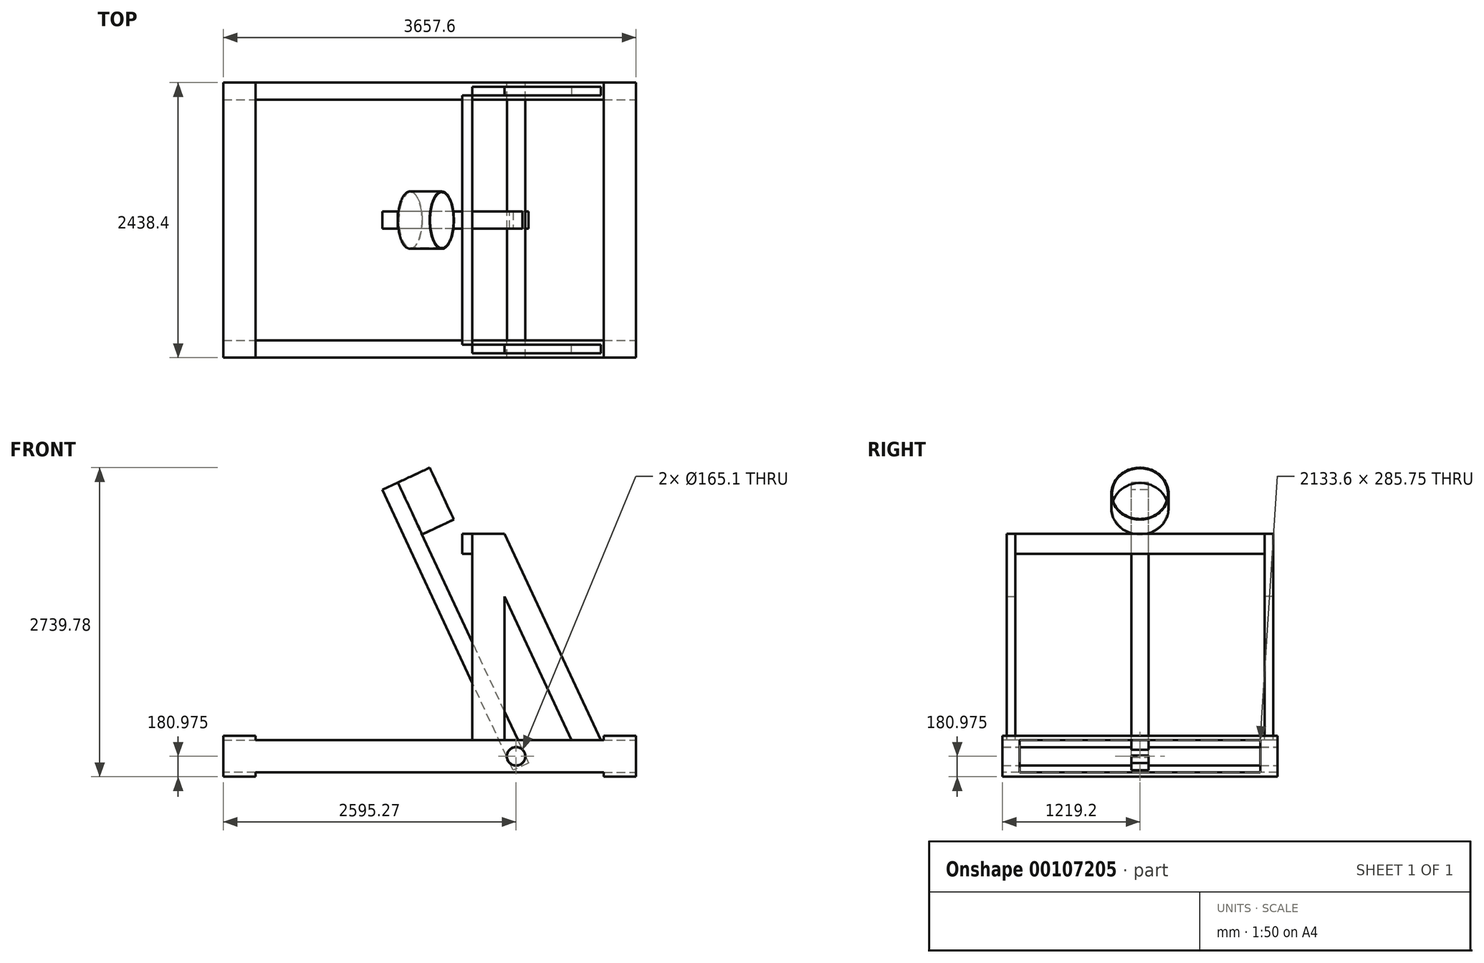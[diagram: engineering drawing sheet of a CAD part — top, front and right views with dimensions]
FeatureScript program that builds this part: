
annotation { "Feature Type Name" : "Feature", "Feature Type Description" : "" }
export const myFeature = defineFeature(function(context is Context, id is Id, definition is map)
    precondition{}
    {
        {
            var Q0;
            Q0=qCreatedBy(makeId("Front.planeOp"),FACE);
            var sketch = newSketch(context, id + "F0", { "sketchPlane" : qUnion([Q0])});
            skLineSegment(sketch, "E0.bottom", {"start": v(0, 0) * mm, "end": v(3657.6, 0) * mm});
            skLineSegment(sketch, "E0.top", {"start": v(0, 285.75) * mm, "end": v(3657.6, 285.75) * mm});
            skLineSegment(sketch, "E0.left", {"start": v(0, 0) * mm, "end": v(0, 285.75) * mm});
            skLineSegment(sketch, "E0.right", {"start": v(3657.6, 0) * mm, "end": v(3657.6, 285.75) * mm});
            skSolve(sketch);
        }
        {
            var Q0;
            Q0 = qSketchRegion(id + "F0", true);
            extrude(context, id + "F1", {"entities" : qUnion([Q0]), "oppositeDirection" : true, "depth" : 152.4 * mm});
        }
        {
            var Q0;
            Q0=makeQuery(id+"F1.opExtrude","SWEPT_FACE",FACE,{"disambiguationData":[OSD([sQuery(id+"F0.wireOp",EDGE,"E0.top")])]});
            var sketch = newSketch(context, id + "F2", { "sketchPlane" : qUnion([Q0])});
            skLineSegment(sketch, "E1.bottom", {"start": v(0, 152.4) * mm, "end": v(285.75, 152.4) * mm});
            skLineSegment(sketch, "E1.top", {"start": v(0, -2286) * mm, "end": v(285.75, -2286) * mm});
            skLineSegment(sketch, "E1.left", {"start": v(0, 152.4) * mm, "end": v(0, -2286) * mm});
            skLineSegment(sketch, "E1.right", {"start": v(285.75, 152.4) * mm, "end": v(285.75, -2286) * mm});
            skSolve(sketch);
        }
        {
            var Q0;
            Q0 = qSketchRegion(id + "F2", true);
            extrude(context, id + "F3", {"entities" : qUnion([Q0]), "operationType" : NewBodyOperationType.ADD, "depth" : 38.1 * mm});
        }
        {
            var Q0;
            Q0=makeQuery(id+"F1.opExtrude","SWEPT_FACE",FACE,{"disambiguationData":[OSD([sQuery(id+"F0.wireOp",EDGE,"E0.bottom")])]});
            var sketch = newSketch(context, id + "F4", { "sketchPlane" : qUnion([Q0])});
            skLineSegment(sketch, "E2.0.0", {"start": v(0, 2286) * mm, "end": v(0, 0) * mm});
            skLineSegment(sketch, "E2.0.1", {"start": v(0, 0) * mm, "end": v(285.75, 0) * mm});
            skLineSegment(sketch, "E2.0.2", {"start": v(285.75, 0) * mm, "end": v(285.75, 2286) * mm});
            skLineSegment(sketch, "E2.0.3", {"start": v(285.75, 2286) * mm, "end": v(0, 2286) * mm});
            skLineSegment(sketch, "E3.0.0", {"start": v(0, -152.4) * mm, "end": v(0, 2286) * mm});
            skLineSegment(sketch, "E3.0.1", {"start": v(0, 2286) * mm, "end": v(285.75, 2286) * mm});
            skLineSegment(sketch, "E3.0.2", {"start": v(285.75, 2286) * mm, "end": v(285.75, -152.4) * mm});
            skLineSegment(sketch, "E3.0.3", {"start": v(285.75, -152.4) * mm, "end": v(0, -152.4) * mm});
            skSolve(sketch);
        }
        {
            var Q0;
            Q0 = qSketchRegion(id + "F4", true);
            extrude(context, id + "F5", {"entities" : qUnion([Q0]), "operationType" : NewBodyOperationType.ADD, "depth" : 38.1 * mm});
        }
        {
            var Q0;
            Q0=makeQuery(id+"F3.opExtrude","SWEPT_FACE",FACE,{"disambiguationData":[OSD([sQuery(id+"F2.wireOp",EDGE,"E1.top")])]});
            var sketch = newSketch(context, id + "F6", { "sketchPlane" : qUnion([Q0])});
            skLineSegment(sketch, "E4.0.0", {"start": v(0, -38.1) * mm, "end": v(0, 323.85) * mm});
            skLineSegment(sketch, "E4.0.1", {"start": v(0, 323.85) * mm, "end": v(285.75, 323.85) * mm});
            skLineSegment(sketch, "E4.0.2", {"start": v(285.75, 323.85) * mm, "end": v(285.75, 285.75) * mm});
            skLineSegment(sketch, "E4.0.3", {"start": v(285.75, 285.75) * mm, "end": v(3657.6, 285.75) * mm});
            skLineSegment(sketch, "E4.0.4", {"start": v(3657.6, 285.75) * mm, "end": v(3657.6, 0) * mm});
            skLineSegment(sketch, "E4.0.5", {"start": v(3657.6, 0) * mm, "end": v(285.75, 0) * mm});
            skLineSegment(sketch, "E4.0.6", {"start": v(285.75, 0) * mm, "end": v(285.75, -38.1) * mm});
            skLineSegment(sketch, "E4.0.7", {"start": v(285.75, -38.1) * mm, "end": v(0, -38.1) * mm});
            skSolve(sketch);
        }
        {
            var Q0;
            {var subQ2=sQuery(id+"F6.wireOp",EDGE,"E4.0.1");Q0=makeQuery(id+"F6.imprint","IMPRINT",FACE,{"disambiguationData":[TD([[makeQuery(id+"F6.imprint","IMPRINT",EDGE,{"derivedFrom":subQ2}),-1.0]])]});}
            var Q1;
            Q1=makeQuery(id+"F6.imprint","IMPRINT",FACE,{"disambiguationData":[TD([[makeQuery(id+"F6.imprint","IMPRINT",EDGE,{"derivedFrom":sQuery(id+"F6.wireOp",EDGE,"E4.0.3")}),-1.0]])]});
            extrude(context, id + "F7", {"entities" : qUnion([Q0, Q1]), "operationType" : NewBodyOperationType.ADD, "oppositeDirection" : true, "depth" : 152.4 * mm});
        }
        {
            var Q0;
            Q0=makeQuery(id+"F7.opExtrude","SWEPT_FACE",FACE,{"disambiguationData":[OSD([sQuery(id+"F6.wireOp",EDGE,"E4.0.4")])]});
            var sketch = newSketch(context, id + "F8", { "sketchPlane" : qUnion([Q0])});
            skLineSegment(sketch, "E5.0.0", {"start": v(-2286, -38.1) * mm, "end": v(152.4, -38.1) * mm});
            skLineSegment(sketch, "E5.0.1", {"start": v(152.4, -38.1) * mm, "end": v(152.4, 0) * mm});
            skLineSegment(sketch, "E5.0.2", {"start": v(152.4, 0) * mm, "end": v(0, 0) * mm});
            skLineSegment(sketch, "E5.0.3", {"start": v(0, 0) * mm, "end": v(-2133.6, 0) * mm});
            skLineSegment(sketch, "E5.0.4", {"start": v(-2133.6, 0) * mm, "end": v(-2286, 0) * mm});
            skLineSegment(sketch, "E5.0.5", {"start": v(-2286, 0) * mm, "end": v(-2286, -38.1) * mm});
            skLineSegment(sketch, "E6.0.0", {"start": v(-2286, 285.75) * mm, "end": v(-2133.6, 285.75) * mm});
            skLineSegment(sketch, "E6.0.1", {"start": v(-2133.6, 285.75) * mm, "end": v(0, 285.75) * mm});
            skLineSegment(sketch, "E6.0.2", {"start": v(0, 285.75) * mm, "end": v(152.4, 285.75) * mm});
            skLineSegment(sketch, "E6.0.3", {"start": v(152.4, 285.75) * mm, "end": v(152.4, 323.85) * mm});
            skLineSegment(sketch, "E6.0.4", {"start": v(152.4, 323.85) * mm, "end": v(-2286, 323.85) * mm});
            skLineSegment(sketch, "E6.0.5", {"start": v(-2286, 323.85) * mm, "end": v(-2286, 285.75) * mm});
            skSolve(sketch);
        }
        {
            var Q0;
            Q0 = qSketchRegion(id + "F8", true);
            extrude(context, id + "F9", {"entities" : qUnion([Q0]), "operationType" : NewBodyOperationType.ADD, "oppositeDirection" : true, "depth" : 285.75 * mm});
        }
        {
            var Q0;
            Q0=makeQuery(id+"F7.opExtrude","CAP_FACE",FACE,{"disambiguationData":[OSD([sQuery(id+"F6.wireOp",EDGE,"E4.0.0"),sQuery(id+"F6.wireOp",EDGE,"E4.0.1"),sQuery(id+"F6.wireOp",EDGE,"E4.0.2"),sQuery(id+"F6.wireOp",EDGE,"E4.0.3"),sQuery(id+"F6.wireOp",EDGE,"E4.0.4"),sQuery(id+"F6.wireOp",EDGE,"E4.0.5"),sQuery(id+"F6.wireOp",EDGE,"E4.0.6"),sQuery(id+"F6.wireOp",EDGE,"E4.0.7")])],"isStart":false});
            var sketch = newSketch(context, id + "F10", { "sketchPlane" : qUnion([Q0])});
            skLineSegment(sketch, "E7.0.0", {"start": v(0, 0) * mm, "end": v(0, 285.75) * mm});
            skLineSegment(sketch, "E7.0.1", {"start": v(0, 285.75) * mm, "end": v(-285.75, 285.75) * mm});
            skLineSegment(sketch, "E7.0.2", {"start": v(-285.75, 285.75) * mm, "end": v(-3371.85, 285.75) * mm});
            skLineSegment(sketch, "E7.0.3", {"start": v(-3371.85, 285.75) * mm, "end": v(-3657.6, 285.75) * mm});
            skLineSegment(sketch, "E7.0.4", {"start": v(-3657.6, 285.75) * mm, "end": v(-3657.6, 0) * mm});
            skLineSegment(sketch, "E7.0.5", {"start": v(-3657.6, 0) * mm, "end": v(-3371.85, 0) * mm});
            skLineSegment(sketch, "E7.0.6", {"start": v(-3371.85, 0) * mm, "end": v(-285.75, 0) * mm});
            skLineSegment(sketch, "E7.0.7", {"start": v(-285.75, 0) * mm, "end": v(0, 0) * mm});
            skLineSegment(sketch, "E8", {"start": v(-2493.67, 2114.55) * mm, "end": v(-2493.67, 0) * mm});
            skLineSegment(sketch, "E9", {"start": v(-2493.67, 2114.55) * mm, "end": v(-2207.92, 2114.55) * mm});
            skLineSegment(sketch, "E10", {"start": v(-2207.92, 2114.55) * mm, "end": v(-2207.92, 0) * mm});
            skLineSegment(sketch, "E11", {"start": v(-2207.92, 0) * mm, "end": v(-2493.67, 0) * mm});
            skLineSegment(sketch, "E12", {"start": v(-3346.45, 285.75) * mm, "end": v(-2493.67, 2114.55) * mm});
            skLineSegment(sketch, "E13", {"start": v(-3346.45, 285.75) * mm, "end": v(-3479.7, 0) * mm});
            skLineSegment(sketch, "E14", {"start": v(-3220.46, 0) * mm, "end": v(-2493.67, 1558.61) * mm});
            skSolve(sketch);
        }
        {
            var Q0;
            {var subQ0=sQuery(id+"F10.wireOp",EDGE,"E9");Q0=makeQuery(id+"F10.imprint","IMPRINT",FACE,{"disambiguationData":[TD([[makeQuery(id+"F10.imprint","IMPRINT",EDGE,{"derivedFrom":subQ0}),-1.0]])]});}
            var Q1;
            {var subQ5=sQuery(id+"F10.wireOp",EDGE,"E11");Q1=makeQuery(id+"F10.imprint","IMPRINT",FACE,{"disambiguationData":[TD([[makeQuery(id+"F10.imprint","IMPRINT",EDGE,{"derivedFrom":subQ5}),1.0]])]});}
            var Q2;
            {var subQ0=sQuery(id+"F10.wireOp",EDGE,"E13");Q2=makeQuery(id+"F10.imprint","IMPRINT",FACE,{"disambiguationData":[TD([[makeQuery(id+"F10.imprint","IMPRINT",EDGE,{"derivedFrom":subQ0}),1.0]])]});}
            var Q3;
            {var subQ0=sQuery(id+"F10.wireOp",EDGE,"E12");Q3=makeQuery(id+"F10.imprint","IMPRINT",FACE,{"disambiguationData":[TD([[makeQuery(id+"F10.imprint","IMPRINT",EDGE,{"derivedFrom":subQ0}),-1.0]])]});}
            extrude(context, id + "F11", {"entities" : qUnion([Q0, Q1, Q2, Q3]), "operationType" : NewBodyOperationType.ADD, "oppositeDirection" : true, "depth" : 114.3 * mm});
        }
        {
            var Q0;
            {var subQ0=sQuery(id+"F10.wireOp",EDGE,"E12");Q0=makeQuery(id+"F10.imprint","IMPRINT",FACE,{"disambiguationData":[TD([[makeQuery(id+"F10.imprint","IMPRINT",EDGE,{"derivedFrom":subQ0}),-1.0]])]});}
            var Q1;
            {var subQ0=sQuery(id+"F10.wireOp",EDGE,"E9");Q1=makeQuery(id+"F10.imprint","IMPRINT",FACE,{"disambiguationData":[TD([[makeQuery(id+"F10.imprint","IMPRINT",EDGE,{"derivedFrom":subQ0}),-1.0]])]});}
            extrude(context, id + "F12", {"entities" : qUnion([Q0, Q1]), "operationType" : NewBodyOperationType.REMOVE, "oppositeDirection" : true, "depth" : 38.1 * mm});
        }
        {
            var Q0;
            Q0=makeQuery(id+"F1.opExtrude","CAP_FACE",FACE,{"disambiguationData":[OSD([sQuery(id+"F0.wireOp",EDGE,"E0.bottom"),sQuery(id+"F0.wireOp",EDGE,"E0.top"),sQuery(id+"F0.wireOp",EDGE,"E0.left"),sQuery(id+"F0.wireOp",EDGE,"E0.right")])],"isStart":true});
            var sketch = newSketch(context, id + "F13", { "sketchPlane" : qUnion([Q0])});
            skLineSegment(sketch, "E15.0.0", {"start": v(2207.92, 2114.55) * mm, "end": v(2207.92, 285.75) * mm});
            skLineSegment(sketch, "E15.0.1", {"start": v(2207.92, 285.75) * mm, "end": v(2493.67, 285.75) * mm});
            skLineSegment(sketch, "E15.0.2", {"start": v(2493.67, 285.75) * mm, "end": v(2493.67, 1558.61) * mm});
            skLineSegment(sketch, "E15.0.3", {"start": v(2493.67, 1558.61) * mm, "end": v(3087.21, 285.75) * mm});
            skLineSegment(sketch, "E15.0.4", {"start": v(3087.21, 285.75) * mm, "end": v(3346.45, 285.75) * mm});
            skLineSegment(sketch, "E15.0.5", {"start": v(3346.45, 285.75) * mm, "end": v(2493.67, 2114.55) * mm});
            skLineSegment(sketch, "E15.0.6", {"start": v(2493.67, 2114.55) * mm, "end": v(2207.92, 2114.55) * mm});
            skSolve(sketch);
        }
        {
            var Q0;
            Q0 = qSketchRegion(id + "F13", true);
            extrude(context, id + "F14", {"entities" : qUnion([Q0]), "operationType" : NewBodyOperationType.ADD, "oppositeDirection" : true, "depth" : 114.3 * mm});
        }
        {
            var Q0;
            Q0=makeQuery(id+"F14.boolean.opBoolean","MERGE",FACE,{"derivedFrom":[makeQuery(id+"F1.opExtrude","CAP_FACE",FACE,{"disambiguationData":[OSD([sQuery(id+"F0.wireOp",EDGE,"E0.bottom"),sQuery(id+"F0.wireOp",EDGE,"E0.top"),sQuery(id+"F0.wireOp",EDGE,"E0.left"),sQuery(id+"F0.wireOp",EDGE,"E0.right")])],"isStart":true}),makeQuery(id+"F14.opExtrude","CAP_FACE",FACE,{"disambiguationData":[OSD([sQuery(id+"F13.wireOp",EDGE,"E15.0.0"),sQuery(id+"F13.wireOp",EDGE,"E15.0.1"),sQuery(id+"F13.wireOp",EDGE,"E15.0.2"),sQuery(id+"F13.wireOp",EDGE,"E15.0.3"),sQuery(id+"F13.wireOp",EDGE,"E15.0.4"),sQuery(id+"F13.wireOp",EDGE,"E15.0.5"),sQuery(id+"F13.wireOp",EDGE,"E15.0.6")])],"isStart":true})]});
            var sketch = newSketch(context, id + "F15", { "sketchPlane" : qUnion([Q0])});
            skLineSegment(sketch, "E16.0.0", {"start": v(2207.92, 2114.55) * mm, "end": v(2207.92, 285.75) * mm});
            skLineSegment(sketch, "E16.0.1", {"start": v(2207.92, 285.75) * mm, "end": v(2493.67, 285.75) * mm});
            skLineSegment(sketch, "E16.0.2", {"start": v(2493.67, 285.75) * mm, "end": v(2493.67, 1558.61) * mm});
            skLineSegment(sketch, "E16.0.3", {"start": v(2493.67, 1558.61) * mm, "end": v(3087.21, 285.75) * mm});
            skLineSegment(sketch, "E16.0.4", {"start": v(3087.21, 285.75) * mm, "end": v(3346.45, 285.75) * mm});
            skLineSegment(sketch, "E16.0.5", {"start": v(3346.45, 285.75) * mm, "end": v(2493.67, 2114.55) * mm});
            skLineSegment(sketch, "E16.0.6", {"start": v(2493.67, 2114.55) * mm, "end": v(2207.92, 2114.55) * mm});
            skSolve(sketch);
        }
        {
            var Q0;
            Q0=makeQuery(id+"F15.imprint","IMPRINT",FACE,{"disambiguationData":[TD([[makeQuery(id+"F15.imprint","IMPRINT",EDGE,{"derivedFrom":sQuery(id+"F15.wireOp",EDGE,"E16.0.0")}),1.0]])]});
            extrude(context, id + "F16", {"entities" : qUnion([Q0]), "operationType" : NewBodyOperationType.REMOVE, "oppositeDirection" : true, "depth" : 38.1 * mm});
        }
        {
            var Q0;
            Q0=makeQuery(id+"F14.opExtrude","SWEPT_FACE",FACE,{"disambiguationData":[OSD([sQuery(id+"F13.wireOp",EDGE,"E15.0.0")])]});
            var sketch = newSketch(context, id + "F17", { "sketchPlane" : qUnion([Q0])});
            skLineSegment(sketch, "E17.0.0", {"start": v(-38.1, 285.75) * mm, "end": v(-38.1, 2114.55) * mm});
            skLineSegment(sketch, "E17.0.1", {"start": v(-38.1, 2114.55) * mm, "end": v(-114.3, 2114.55) * mm});
            skLineSegment(sketch, "E17.0.2", {"start": v(-114.3, 2114.55) * mm, "end": v(-114.3, 285.75) * mm});
            skLineSegment(sketch, "E17.0.3", {"start": v(-114.3, 285.75) * mm, "end": v(-38.1, 285.75) * mm});
            skLineSegment(sketch, "E18.0.0", {"start": v(2247.9, 2114.55) * mm, "end": v(2171.7, 2114.55) * mm});
            skLineSegment(sketch, "E18.0.1", {"start": v(2171.7, 2114.55) * mm, "end": v(2171.7, 285.75) * mm});
            skLineSegment(sketch, "E18.0.2", {"start": v(2171.7, 285.75) * mm, "end": v(2247.9, 285.75) * mm});
            skLineSegment(sketch, "E18.0.3", {"start": v(2247.9, 285.75) * mm, "end": v(2247.9, 2114.55) * mm});
            skLineSegment(sketch, "E19.bottom", {"start": v(-114.3, 2114.55) * mm, "end": v(2247.9, 2114.55) * mm});
            skLineSegment(sketch, "E19.top", {"start": v(-114.3, 1936.75) * mm, "end": v(2247.9, 1936.75) * mm});
            skLineSegment(sketch, "E19.left", {"start": v(-114.3, 2114.55) * mm, "end": v(-114.3, 1936.75) * mm});
            skLineSegment(sketch, "E19.right", {"start": v(2247.9, 2114.55) * mm, "end": v(2247.9, 1936.75) * mm});
            skSolve(sketch);
        }
        {
            var Q0;
            {var subQ5=sQuery(id+"F17.wireOp",EDGE,"E19.left");Q0=makeQuery(id+"F17.imprint","IMPRINT",FACE,{"disambiguationData":[TD([[makeQuery(id+"F17.imprint","IMPRINT",EDGE,{"derivedFrom":subQ5}),1.0]])]});}
            var Q1;
            {var subQ5=sQuery(id+"F17.wireOp",EDGE,"E19.right");Q1=makeQuery(id+"F17.imprint","IMPRINT",FACE,{"disambiguationData":[TD([[makeQuery(id+"F17.imprint","IMPRINT",EDGE,{"derivedFrom":subQ5}),-1.0]])]});}
            var Q2;
            {var subQ0=sQuery(id+"F17.wireOp",EDGE,"E19.bottom");var subQ1=sQuery(id+"F17.wireOp",EDGE,"E17.0.0");var subQ2=makeQuery(id+"F17.imprint","INTERSECT",VERTEX,{"derivedFrom":[subQ1,subQ0]});Q2=makeQuery(id+"F17.imprint","IMPRINT",FACE,{"disambiguationData":[TD([[makeQuery(id+"F17.imprint","IMPRINT",EDGE,{"disambiguationData":[TD([[subQ2,-1.0]])],"derivedFrom":subQ1}),1.0]])]});}
            extrude(context, id + "F18", {"entities" : qUnion([Q0, Q1, Q2]), "operationType" : NewBodyOperationType.ADD, "depth" : 88.9 * mm});
        }
        {
            var Q0;
            Q0=makeQuery(id+"F9.boolean.opBoolean","MERGE",FACE,{"derivedFrom":[makeQuery(id+"F5.boolean.opBoolean","MERGE",FACE,{"derivedFrom":[makeQuery(id+"F3.boolean.opBoolean","MERGE",FACE,{"derivedFrom":[makeQuery(id+"F1.opExtrude","CAP_FACE",FACE,{"disambiguationData":[OSD([sQuery(id+"F0.wireOp",EDGE,"E0.bottom"),sQuery(id+"F0.wireOp",EDGE,"E0.top"),sQuery(id+"F0.wireOp",EDGE,"E0.left"),sQuery(id+"F0.wireOp",EDGE,"E0.right")])],"isStart":false}),makeQuery(id+"F3.opExtrude","SWEPT_FACE",FACE,{"disambiguationData":[OSD([sQuery(id+"F2.wireOp",EDGE,"E1.bottom")])]})]}),makeQuery(id+"F5.opExtrude","SWEPT_FACE",FACE,{"disambiguationData":[OSD([sQuery(id+"F4.wireOp",EDGE,"E3.0.3")])]})]}),makeQuery(id+"F9.opExtrude","SWEPT_FACE",FACE,{"disambiguationData":[OSD([sQuery(id+"F8.wireOp",EDGE,"E5.0.1")])]}),makeQuery(id+"F9.opExtrude","SWEPT_FACE",FACE,{"disambiguationData":[OSD([sQuery(id+"F8.wireOp",EDGE,"E6.0.3")])]})]});
            var sketch = newSketch(context, id + "F19", { "sketchPlane" : qUnion([Q0])});
            skLineSegment(sketch, "E20.0.0", {"start": v(0, -38.1) * mm, "end": v(0, 323.85) * mm});
            skLineSegment(sketch, "E20.0.1", {"start": v(0, 323.85) * mm, "end": v(-285.75, 323.85) * mm});
            skLineSegment(sketch, "E20.0.2", {"start": v(-285.75, 323.85) * mm, "end": v(-285.75, 285.75) * mm});
            skLineSegment(sketch, "E20.0.3", {"start": v(-285.75, 285.75) * mm, "end": v(-3371.85, 285.75) * mm});
            skLineSegment(sketch, "E20.0.4", {"start": v(-3371.85, 285.75) * mm, "end": v(-3371.85, 323.85) * mm});
            skLineSegment(sketch, "E20.0.5", {"start": v(-3371.85, 323.85) * mm, "end": v(-3657.6, 323.85) * mm});
            skLineSegment(sketch, "E20.0.6", {"start": v(-3657.6, 323.85) * mm, "end": v(-3657.6, -38.1) * mm});
            skLineSegment(sketch, "E20.0.7", {"start": v(-3657.6, -38.1) * mm, "end": v(-3371.85, -38.1) * mm});
            skLineSegment(sketch, "E20.0.8", {"start": v(-3371.85, -38.1) * mm, "end": v(-3371.85, 0) * mm});
            skLineSegment(sketch, "E20.0.9", {"start": v(-3371.85, 0) * mm, "end": v(-285.75, 0) * mm});
            skLineSegment(sketch, "E20.0.10", {"start": v(-285.75, 0) * mm, "end": v(-285.75, -38.1) * mm});
            skLineSegment(sketch, "E20.0.11", {"start": v(-285.75, -38.1) * mm, "end": v(0, -38.1) * mm});
            skLineSegment(sketch, "E21.0.0", {"start": v(-2119.02, 2114.55) * mm, "end": v(-2493.67, 2114.55) * mm});
            skLineSegment(sketch, "E21.0.1", {"start": v(-2493.67, 2114.55) * mm, "end": v(-3346.45, 285.75) * mm});
            skLineSegment(sketch, "E21.0.2", {"start": v(-3346.45, 285.75) * mm, "end": v(-3087.21, 285.75) * mm});
            skLineSegment(sketch, "E21.0.3", {"start": v(-3087.21, 285.75) * mm, "end": v(-2493.67, 1558.61) * mm});
            skLineSegment(sketch, "E21.0.4", {"start": v(-2493.67, 1558.61) * mm, "end": v(-2493.67, 285.75) * mm});
            skLineSegment(sketch, "E21.0.5", {"start": v(-2493.67, 285.75) * mm, "end": v(-2207.92, 285.75) * mm});
            skLineSegment(sketch, "E21.0.6", {"start": v(-2207.92, 285.75) * mm, "end": v(-2207.92, 1936.75) * mm});
            skLineSegment(sketch, "E21.0.7", {"start": v(-2207.92, 1936.75) * mm, "end": v(-2119.02, 1936.75) * mm});
            skLineSegment(sketch, "E21.0.8", {"start": v(-2119.02, 1936.75) * mm, "end": v(-2119.02, 2114.55) * mm});
            skCircle(sketch, "E22", {"center": v(-2595.27, 142.88) * mm, "radius": 82.55 * mm});
            skPoint(sketch, "E22.centerSnap0", {"position": v(-3657.6, 142.88) * mm});
            skSolve(sketch);
        }
        {
            var Q0;
            Q0=makeQuery(id+"F19.imprint","IMPRINT",FACE,{"disambiguationData":[TD([[makeQuery(id+"F19.imprint","IMPRINT",EDGE,{"derivedFrom":sQuery(id+"F19.wireOp",EDGE,"E22")}),1.0]])]});
            extrude(context, id + "F20", {"entities" : qUnion([Q0]), "operationType" : NewBodyOperationType.REMOVE, "endBound" : BoundingType.THROUGH_ALL, "oppositeDirection" : true, "depth" : 25.4 * mm});
        }
        {
            var Q0;
            Q0=makeQuery(id+"F9.boolean.opBoolean","MERGE",FACE,{"derivedFrom":[makeQuery(id+"F5.boolean.opBoolean","MERGE",FACE,{"derivedFrom":[makeQuery(id+"F3.boolean.opBoolean","MERGE",FACE,{"derivedFrom":[makeQuery(id+"F1.opExtrude","CAP_FACE",FACE,{"disambiguationData":[OSD([sQuery(id+"F0.wireOp",EDGE,"E0.bottom"),sQuery(id+"F0.wireOp",EDGE,"E0.top"),sQuery(id+"F0.wireOp",EDGE,"E0.left"),sQuery(id+"F0.wireOp",EDGE,"E0.right")])],"isStart":false}),makeQuery(id+"F3.opExtrude","SWEPT_FACE",FACE,{"disambiguationData":[OSD([sQuery(id+"F2.wireOp",EDGE,"E1.bottom")])]})]}),makeQuery(id+"F5.opExtrude","SWEPT_FACE",FACE,{"disambiguationData":[OSD([sQuery(id+"F4.wireOp",EDGE,"E3.0.3")])]})]}),makeQuery(id+"F9.opExtrude","SWEPT_FACE",FACE,{"disambiguationData":[OSD([sQuery(id+"F8.wireOp",EDGE,"E5.0.1")])]}),makeQuery(id+"F9.opExtrude","SWEPT_FACE",FACE,{"disambiguationData":[OSD([sQuery(id+"F8.wireOp",EDGE,"E6.0.3")])]})]});
            var sketch = newSketch(context, id + "F21", { "sketchPlane" : qUnion([Q0])});
            skCircle(sketch, "E23.0", {"center": v(-2595.27, 142.88) * mm, "radius": 82.55 * mm});
            skCircle(sketch, "E24", {"center": v(-2595.27, 142.88) * mm, "radius": 80.96 * mm});
            skSolve(sketch);
        }
        {
            var Q0;
            Q0=makeQuery(id+"F21.imprint","IMPRINT",FACE,{"disambiguationData":[TD([[makeQuery(id+"F21.imprint","IMPRINT",EDGE,{"derivedFrom":sQuery(id+"F21.wireOp",EDGE,"E24")}),1.0]])]});
            var Q1;
            Q1=makeQuery(id+"F9.boolean.opBoolean","MERGE",FACE,{"derivedFrom":[makeQuery(id+"F7.boolean.opBoolean","MERGE",FACE,{"derivedFrom":[makeQuery(id+"F3.opExtrude","SWEPT_FACE",FACE,{"disambiguationData":[OSD([sQuery(id+"F2.wireOp",EDGE,"E1.top")])]}),makeQuery(id+"F5.opExtrude","SWEPT_FACE",FACE,{"disambiguationData":[OSD([sQuery(id+"F4.wireOp",EDGE,"E3.0.1")])]}),makeQuery(id+"F7.opExtrude","CAP_FACE",FACE,{"disambiguationData":[OSD([sQuery(id+"F6.wireOp",EDGE,"E4.0.0"),sQuery(id+"F6.wireOp",EDGE,"E4.0.1"),sQuery(id+"F6.wireOp",EDGE,"E4.0.2"),sQuery(id+"F6.wireOp",EDGE,"E4.0.3"),sQuery(id+"F6.wireOp",EDGE,"E4.0.4"),sQuery(id+"F6.wireOp",EDGE,"E4.0.5"),sQuery(id+"F6.wireOp",EDGE,"E4.0.6"),sQuery(id+"F6.wireOp",EDGE,"E4.0.7")])],"isStart":true})]}),makeQuery(id+"F9.opExtrude","SWEPT_FACE",FACE,{"disambiguationData":[OSD([sQuery(id+"F8.wireOp",EDGE,"E5.0.5")])]}),makeQuery(id+"F9.opExtrude","SWEPT_FACE",FACE,{"disambiguationData":[OSD([sQuery(id+"F8.wireOp",EDGE,"E6.0.5")])]})]});
            extrude(context, id + "F22", {"entities" : qUnion([Q0]), "endBound" : BoundingType.UP_TO_SURFACE, "oppositeDirection" : true, "endBoundEntityFace" : qUnion([Q1]), "depth" : 25.4 * mm});
        }
        {
            var Q0;
            Q0=makeQuery(id+"F11.boolean.opBoolean","MERGE",FACE,{"derivedFrom":[makeQuery(id+"F7.opExtrude","CAP_FACE",FACE,{"disambiguationData":[OSD([sQuery(id+"F6.wireOp",EDGE,"E4.0.0"),sQuery(id+"F6.wireOp",EDGE,"E4.0.1"),sQuery(id+"F6.wireOp",EDGE,"E4.0.2"),sQuery(id+"F6.wireOp",EDGE,"E4.0.3"),sQuery(id+"F6.wireOp",EDGE,"E4.0.4"),sQuery(id+"F6.wireOp",EDGE,"E4.0.5"),sQuery(id+"F6.wireOp",EDGE,"E4.0.6"),sQuery(id+"F6.wireOp",EDGE,"E4.0.7")])],"isStart":false}),makeQuery(id+"F11.opExtrude","CAP_FACE",FACE,{"disambiguationData":[OSD([sQuery(id+"F10.wireOp",EDGE,"E7.0.5"),sQuery(id+"F10.wireOp",EDGE,"E7.0.6"),sQuery(id+"F10.wireOp",EDGE,"E8"),sQuery(id+"F10.wireOp",EDGE,"E9"),sQuery(id+"F10.wireOp",EDGE,"E10"),sQuery(id+"F10.wireOp",EDGE,"E11"),sQuery(id+"F10.wireOp",EDGE,"E12"),sQuery(id+"F10.wireOp",EDGE,"E13"),sQuery(id+"F10.wireOp",EDGE,"E14")])],"isStart":true})]});
            cPlane(context, id + "F23", {"entities" : qUnion([Q0]), "cplaneType" : CPlaneType.OFFSET, "offset" : 990.6 * mm, "width" : 152.4 * mm, "height" : 152.4 * mm});
        }
        {
            var Q0;
            Q0=qCreatedBy(id+"F23.planeOp",FACE);
            var sketch = newSketch(context, id + "F24", { "sketchPlane" : qUnion([Q0])});
            skCircle(sketch, "E25.0.0", {"center": v(-2595.27, 142.88) * mm, "radius": 80.96 * mm});
            skLineSegment(sketch, "E26.0.0", {"start": v(-2119.02, 2114.55) * mm, "end": v(-2493.67, 2114.55) * mm});
            skLineSegment(sketch, "E26.0.1", {"start": v(-2493.67, 2114.55) * mm, "end": v(-3346.45, 285.75) * mm});
            skLineSegment(sketch, "E26.0.2", {"start": v(-3346.45, 285.75) * mm, "end": v(-3087.21, 285.75) * mm});
            skLineSegment(sketch, "E26.0.3", {"start": v(-3087.21, 285.75) * mm, "end": v(-2493.67, 1558.61) * mm});
            skLineSegment(sketch, "E26.0.4", {"start": v(-2493.67, 1558.61) * mm, "end": v(-2493.67, 285.75) * mm});
            skLineSegment(sketch, "E26.0.5", {"start": v(-2493.67, 285.75) * mm, "end": v(-2207.92, 285.75) * mm});
            skLineSegment(sketch, "E26.0.6", {"start": v(-2207.92, 285.75) * mm, "end": v(-2207.92, 1936.75) * mm});
            skLineSegment(sketch, "E26.0.7", {"start": v(-2207.92, 1936.75) * mm, "end": v(-2119.02, 1936.75) * mm});
            skLineSegment(sketch, "E26.0.8", {"start": v(-2119.02, 1936.75) * mm, "end": v(-2119.02, 2114.55) * mm});
            skLineSegment(sketch, "E27", {"start": v(-2595.27, 142.88) * mm, "end": v(-2663.85, 176.08) * mm});
            skLineSegment(sketch, "E28", {"start": v(-2663.85, 176.08) * mm, "end": v(-1547.46, 2570.18) * mm});
            skLineSegment(sketch, "E29", {"start": v(-2663.85, 176.08) * mm, "end": v(-2706.79, 84) * mm});
            skLineSegment(sketch, "E30", {"start": v(-2706.79, 84) * mm, "end": v(-2568.67, 19.6) * mm});
            skLineSegment(sketch, "E31", {"start": v(-2568.67, 19.6) * mm, "end": v(-1409.34, 2505.78) * mm});
            skLineSegment(sketch, "E32", {"start": v(-1409.34, 2505.78) * mm, "end": v(-1547.46, 2570.18) * mm});
            skSolve(sketch);
        }
        {
            var Q0;
            {var subQ0=sQuery(id+"F24.wireOp",EDGE,"E29");var subQ1=sQuery(id+"F24.wireOp",EDGE,"E25.0.0");var subQ2=makeQuery(id+"F24.imprint","INTERSECT",VERTEX,{"derivedFrom":[subQ1,subQ0]});Q0=makeQuery(id+"F24.imprint","IMPRINT",FACE,{"disambiguationData":[TD([[makeQuery(id+"F24.imprint","IMPRINT",EDGE,{"disambiguationData":[TD([[subQ2,1.0]])],"derivedFrom":subQ1}),1.0]])]});}
            var Q1;
            {var subQ5=sQuery(id+"F24.wireOp",EDGE,"E30");Q1=makeQuery(id+"F24.imprint","IMPRINT",FACE,{"disambiguationData":[TD([[makeQuery(id+"F24.imprint","IMPRINT",EDGE,{"derivedFrom":subQ5}),1.0]])]});}
            var Q2;
            {var subQ0=sQuery(id+"F24.wireOp",EDGE,"E31");var subQ1=sQuery(id+"F24.wireOp",EDGE,"E25.0.0");var subQ2=makeQuery(id+"F24.imprint","INTERSECT",VERTEX,{"disambiguationData":[OD(0.0)],"derivedFrom":[subQ1,subQ0]});Q2=makeQuery(id+"F24.imprint","IMPRINT",FACE,{"disambiguationData":[TD([[makeQuery(id+"F24.imprint","IMPRINT",EDGE,{"disambiguationData":[TD([[subQ2,-1.0]])],"derivedFrom":subQ1}),1.0]])]});}
            var Q3;
            {var subQ5=sQuery(id+"F24.wireOp",EDGE,"E32");Q3=makeQuery(id+"F24.imprint","IMPRINT",FACE,{"disambiguationData":[TD([[makeQuery(id+"F24.imprint","IMPRINT",EDGE,{"derivedFrom":subQ5}),1.0]])]});}
            var Q4;
            {var subQ3=sQuery(id+"F24.wireOp",EDGE,"E28");var subQ5=sQuery(id+"F24.wireOp",EDGE,"E25.0.0");var subQ6=makeQuery(id+"F24.imprint","INTERSECT",VERTEX,{"derivedFrom":[subQ5,subQ3]});Q4=makeQuery(id+"F24.imprint","IMPRINT",FACE,{"disambiguationData":[TD([[makeQuery(id+"F24.imprint","IMPRINT",EDGE,{"disambiguationData":[TD([[subQ6,1.0]])],"derivedFrom":subQ5}),-1.0]])]});}
            var Q5;
            {var subQ1=sQuery(id+"F24.wireOp",EDGE,"E25.0.0");var subQ5=sQuery(id+"F24.wireOp",EDGE,"E29");var subQ7=makeQuery(id+"F24.imprint","INTERSECT",VERTEX,{"derivedFrom":[subQ1,subQ5]});Q5=makeQuery(id+"F24.imprint","IMPRINT",FACE,{"disambiguationData":[TD([[makeQuery(id+"F24.imprint","IMPRINT",EDGE,{"disambiguationData":[TD([[subQ7,-1.0]])],"derivedFrom":subQ1}),1.0]])]});}
            var Q6;
            {var subQ1=sQuery(id+"F24.wireOp",EDGE,"E26.0.4");var subQ5=sQuery(id+"F24.wireOp",EDGE,"E26.0.5");var subQ6=makeQuery(id+"F24.imprint","INTERSECT",VERTEX,{"derivedFrom":[subQ1,subQ5]});Q6=makeQuery(id+"F24.imprint","IMPRINT",FACE,{"disambiguationData":[TD([[makeQuery(id+"F24.imprint","IMPRINT",EDGE,{"disambiguationData":[TD([[subQ6,1.0]])],"derivedFrom":subQ1}),1.0]])]});}
            extrude(context, id + "F25", {"entities" : qUnion([Q0, Q1, Q2, Q3, Q4, Q5, Q6]), "operationType" : NewBodyOperationType.ADD, "depth" : 152.4 * mm});
        }
        {
            var Q0;
            Q0=makeQuery(id+"F25.opExtrude","SWEPT_FACE",FACE,{"disambiguationData":[OSD([sQuery(id+"F24.wireOp",EDGE,"E28")])]});
            var sketch = newSketch(context, id + "F26", { "sketchPlane" : qUnion([Q0])});
            skCircle(sketch, "E33", {"center": v(-1066.8, 1421.4) * mm, "radius": 254 * mm});
            skPoint(sketch, "E33.centerSnap0", {"position": v(-1066.8, 1675.4) * mm});
            skSolve(sketch);
        }
        {
            var Q0;
            Q0 = qSketchRegion(id + "F26", true);
            extrude(context, id + "F27", {"entities" : qUnion([Q0]), "operationType" : NewBodyOperationType.ADD, "depth" : 6.35 * mm});
        }
        {
            var Q0;
            Q0=makeQuery(id+"F27.opExtrude","CAP_FACE",FACE,{"disambiguationData":[OSD([sQuery(id+"F26.wireOp",EDGE,"E33")])],"isStart":false});
            var sketch = newSketch(context, id + "F28", { "sketchPlane" : qUnion([Q0])});
            skCircle(sketch, "E34.0.0", {"center": v(-1066.8, 1421.4) * mm, "radius": 254 * mm});
            skCircle(sketch, "E35", {"center": v(-1066.8, 1421.4) * mm, "radius": 247.65 * mm});
            skSolve(sketch);
        }
        {
            var Q0;
            Q0 = qSketchRegion(id + "F28", true);
            extrude(context, id + "F29", {"entities" : qUnion([Q0]), "operationType" : NewBodyOperationType.ADD, "depth" : 304.8 * mm});
        }
    });
